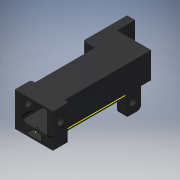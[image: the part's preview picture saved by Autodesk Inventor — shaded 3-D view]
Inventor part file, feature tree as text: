
AUTODESK INVENTOR PART (.ipt)
format: ipt  version: 2016 (Build 200138000, 138)  size: 412,672 bytes
history: native  units: mm
features: extrude x18, sketch x18, fillet x5
ambient origin geometry x8: Origin, YZ Plane, XZ Plane, XY Plane, X Axis, Y Axis, Z Axis, Center Point
bodies: Solid1 (feature_tree)
feature tree (41):
  extrude  "Extrusion1"  Depth=13.0mm
  extrude  "Extrusion2"  Depth=15.0mm
  extrude  "Extrusion3"  Depth=5.0mm
  extrude  "Extrusion7"  Depth=1.0mm TaperAngle=0.0deg
  extrude  "Extrusion9"  Depth=47.0mm
  extrude  "Extrusion10"  Depth=3.0mm
  extrude  "Extrusion11"  Depth=7.0mm
  extrude  "Extrusion15"  Depth=4.0mm
  sketch  "Sketch17"  dims[d39=10.0mm d40=0.0mm d47=1.0mm]
  fillet  "Fillet11"  Radius=8.0mm
  extrude  "Extrusion18"  Depth=1.0mm
  extrude  "Extrusion19"  Depth=1.0mm TaperAngle=0.0deg
  extrude  "Extrusion28"  Depth=5.0mm
  extrude  "Extrusion29"  TaperAngle=0.0deg  [1 undecoded]
  extrude  "Extrusion35"  Depth=15.0mm TaperAngle=0.0deg
  extrude  "Extrusion36"  Depth=8.0mm
  fillet  "Fillet20"  Radius=7.0mm
  extrude  "Extrusion38"  Depth=2.0mm
  extrude  "Extrusion39"  Depth=6.0mm TaperAngle=0.0deg
  fillet  "Fillet21"  Radius=4.0mm
  extrude  "Extrusion40"  Depth=8.0mm
  fillet  "Fillet24"  Radius=4.45mm
  extrude  "Extrusion41"  Depth=3.0mm
  fillet  "Fillet25"  Radius=1.4mm
  sketch  "Sketch1"  dims[d2=11.0mm d3=13.0mm]
  sketch  "Sketch2"  dims[d6=13.0mm d7=15.0mm]
  sketch  "Sketch3"  dims[d8=50.0mm d9=0.0mm d10=5.0mm]
  sketch  "Sketch7"  dims[d14=1.5mm d15=1.0mm d16=0.0mm]
  sketch  "Sketch9"  dims[d17=47.0mm d18=3.2mm]
  sketch  "Sketch11"  dims[d19=50.0mm d20=0.0mm d33=3.0mm]
  sketch  "Sketch12"  dims[d34=8.0mm d35=7.0mm]
  sketch  "Sketch16"  dims[d36=4.0mm d37=4.0mm d38=8.0mm]
  sketch  "Sketch21"  dims[d48=1.0mm d49=1.0mm d50=0.0mm]
  sketch  "Sketch31"  dims[d51=7.5mm d52=5.0mm]
  sketch  "Sketch32"  dims[d53=1.0mm d54=0.0mm d55=0.0mm]
  sketch  "Sketch39"  dims[d56=3.0mm d57=15.0mm d58=0.0mm]
  sketch  "Sketch40"  dims[d75=2.0mm d76=0.0mm d78=8.0mm d92=7.0mm]
  sketch  "Sketch42"  dims[d93=5.0mm d97=2.0mm]
  sketch  "Sketch43"  dims[d98=2.0mm d99=0.0mm d108=6.0mm d109=0.0mm d144=4.0mm]
  sketch  "Sketch44"  dims[d145=4.0mm d147=8.0mm d150=4.45mm]
  sketch  "Sketch46"  dims[d151=1.4mm d153=4.45mm d154=1.4mm d155=2.0mm d156=0.0mm d160=10.0mm d162=3.5mm d164=3.0mm d165=0.0mm d218=1.0mm d219=3.0mm d220=0.0mm d221=1.0mm d222=0.0mm d224=1.0mm d230=5.0mm d231=3.0mm d232=5.0mm d233=0.0mm d234=1.0mm d235=6.0mm d236=3.5mm d237=3.0mm d238=2.0mm d239=15.0mm d240=0.0mm d241=1.0mm d242=3.0mm d243=3.0mm d250=2.0mm d251=0.0mm d252=3.0mm d253=10.3mm d255=1.0mm d256=1.0mm d257=1.0mm d264=1.0mm d265=0.0mm d266=3.0mm]
note: 1 required parameter value undecoded (feature->parameter linkage not recoverable at this tier; creation-order binding heuristic only, values carry confidence <= 0.55)
